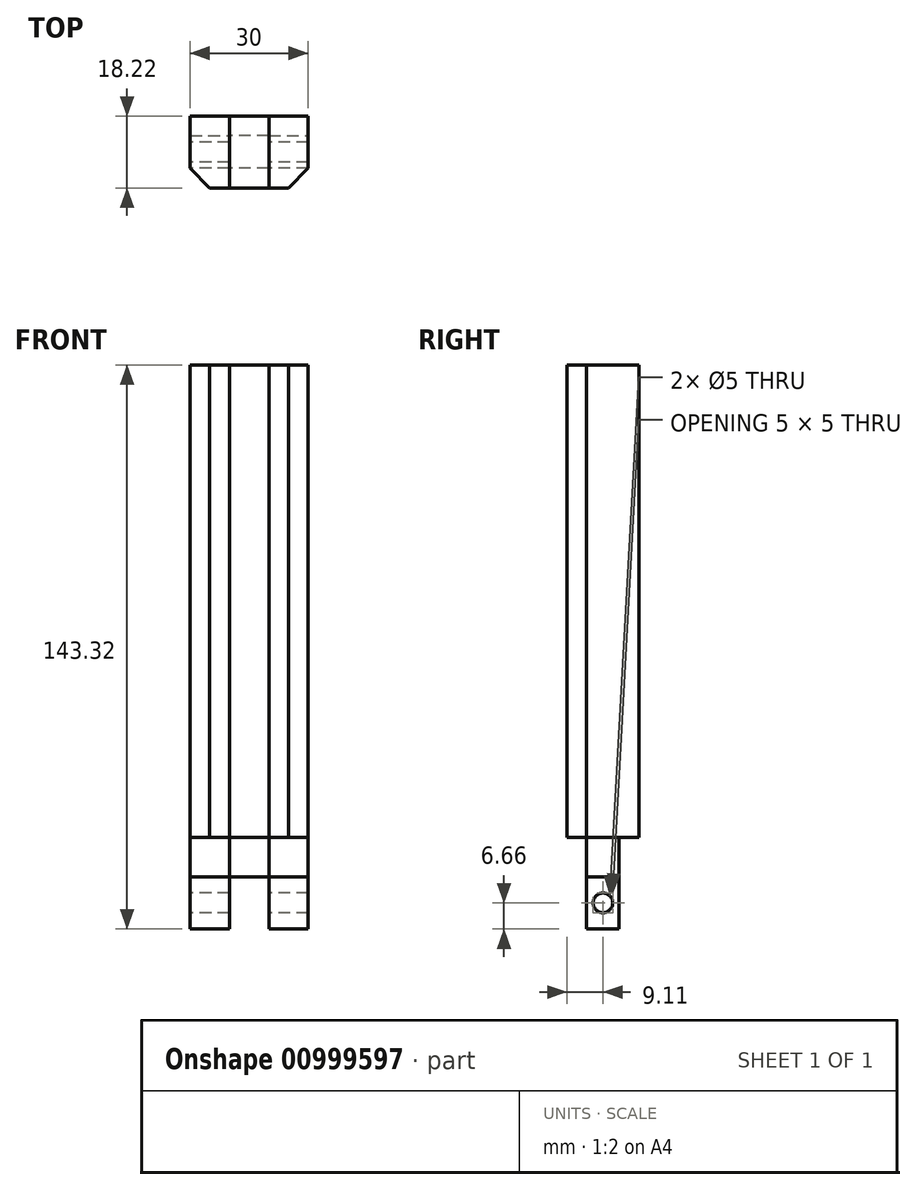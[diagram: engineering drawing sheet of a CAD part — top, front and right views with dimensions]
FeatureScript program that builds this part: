
annotation { "Feature Type Name" : "Feature", "Feature Type Description" : "" }
export const myFeature = defineFeature(function(context is Context, id is Id, definition is map)
    precondition{}
    {
        {
            var Q0;
            Q0=qCreatedBy(makeId("Right.planeOp"),FACE);
            var sketch = newSketch(context, id + "F0", { "sketchPlane" : qUnion([Q0])});
            skCircle(sketch, "E0", {"center": v(0, 0) * mm, "radius": 2.5 * mm});
            skSolve(sketch);
        }
        {
            var Q0;
            Q0=makeQuery(id+"F0.imprint","IMPRINT",FACE,{"disambiguationData":[TD([[makeQuery(id+"F0.imprint","IMPRINT",EDGE,{"derivedFrom":sQuery(id+"F0.wireOp",EDGE,"E0")}),1.0]])]});
            var sketch = newSketch(context, id + "F1", { "sketchPlane" : qUnion([Q0])});
            skLineSegment(sketch, "E1.bottom", {"start": v(9.11, 6.66) * mm, "end": v(-9.11, 6.66) * mm});
            skLineSegment(sketch, "E1.top", {"start": v(9.11, -6.66) * mm, "end": v(-9.11, -6.66) * mm});
            skLineSegment(sketch, "E1.left", {"start": v(9.11, 6.66) * mm, "end": v(9.11, -6.66) * mm});
            skLineSegment(sketch, "E1.right", {"start": v(-9.11, 6.66) * mm, "end": v(-9.11, -6.66) * mm});
            skPoint(sketch, "E1.middle", {"position": v(0, 0) * mm});
            skSolve(sketch);
        }
        {
            var Q0;
            Q0=makeQuery(id+"F1.imprint","IMPRINT",FACE,{"disambiguationData":[TD([[makeQuery(id+"F1.imprint","IMPRINT",EDGE,{"derivedFrom":sQuery(id+"F1.wireOp",EDGE,"E1.bottom")}),1.0]])]});
            extrude(context, id + "F2", {"entities" : qUnion([Q0]), "depth" : 30 * mm, "offsetDistance" : 25 * mm});
        }
        {
            var Q0;
            Q0=makeQuery(id+"F2.opExtrude","SWEPT_FACE",FACE,{"disambiguationData":[OSD([sQuery(id+"F1.wireOp",EDGE,"E1.bottom")])]});
            var sketch = newSketch(context, id + "F3", { "sketchPlane" : qUnion([Q0])});
            skLineSegment(sketch, "E2", {"start": v(10, 9.11) * mm, "end": v(10, -9.11) * mm});
            skLineSegment(sketch, "E3", {"start": v(20, 9.11) * mm, "end": v(20, -9.11) * mm});
            skSolve(sketch);
        }
        {
            var Q0;
            {var subQ0=sQuery(id+"F3.wireOp",EDGE,"E2");Q0=makeQuery(id+"F3.imprint","IMPRINT",FACE,{"disambiguationData":[TD([[makeQuery(id+"F3.imprint","IMPRINT",EDGE,{"derivedFrom":subQ0}),1.0]])]});}
            extrude(context, id + "F4", {"entities" : qUnion([Q0]), "operationType" : NewBodyOperationType.REMOVE, "oppositeDirection" : true, "depth" : 25 * mm, "offsetDistance" : 25 * mm});
        }
        {
            var Q0;
            {var subQ2=sQuery(id+"F1.wireOp",EDGE,"E1.bottom");Q0=makeQuery(id+"F4.boolean.opBoolean","SPLIT",FACE,{"disambiguationData":[TD([makeQuery(id+"F4.opExtrude","SWEPT_FACE",FACE,{"disambiguationData":[OSD([sQuery(id+"F3.wireOp",EDGE,"E2")])]})])],"derivedFrom":makeQuery(id+"F2.opExtrude","SWEPT_FACE",FACE,{"disambiguationData":[OSD([subQ2])]})});}
            var Q1;
            {var subQ2=sQuery(id+"F1.wireOp",EDGE,"E1.bottom");Q1=makeQuery(id+"F4.boolean.opBoolean","SPLIT",FACE,{"disambiguationData":[TD([makeQuery(id+"F4.opExtrude","SWEPT_FACE",FACE,{"disambiguationData":[OSD([sQuery(id+"F3.wireOp",EDGE,"E3")])]})])],"derivedFrom":makeQuery(id+"F2.opExtrude","SWEPT_FACE",FACE,{"disambiguationData":[OSD([subQ2])]})});}
            extrude(context, id + "F5", {"entities" : qUnion([Q0, Q1]), "depth" : 10 * mm, "offsetDistance" : 25 * mm});
        }
        {
            var Q0;
            Q0=makeQuery(id+"F5.opExtrude","SWEPT_FACE",FACE,{"disambiguationData":[OSD([sQuery(id+"F3.wireOp",EDGE,"E2")])]});
            extrude(context, id + "F6", {"entities" : qUnion([Q0]), "depth" : 10 * mm, "offsetDistance" : 25 * mm});
        }
        {
            var Q0;
            {var subQ2=sQuery(id+"F1.wireOp",EDGE,"E1.bottom");Q0=makeQuery(id+"F5.opExtrude","CAP_FACE",FACE,{"disambiguationData":[OSD([subQ2]),TDD([makeQuery(id+"F4.boolean.opBoolean","SPLIT",FACE,{"disambiguationData":[TD([makeQuery(id+"F4.opExtrude","SWEPT_FACE",FACE,{"disambiguationData":[OSD([sQuery(id+"F3.wireOp",EDGE,"E2")])]})])],"derivedFrom":makeQuery(id+"F2.opExtrude","SWEPT_FACE",FACE,{"disambiguationData":[OSD([subQ2])]})})])],"isStart":false});}
            var Q1;
            {var subQ0=sQuery(id+"F3.wireOp",EDGE,"E2");Q1=makeQuery(id+"F6.opExtrude","SWEPT_FACE",FACE,{"disambiguationData":[OSD([subQ0]),TDD([makeQuery(id+"F5.opExtrude","CAP_EDGE",EDGE,{"disambiguationData":[OSD([subQ0])],"isStart":false})])]});}
            var Q2;
            {var subQ2=sQuery(id+"F1.wireOp",EDGE,"E1.bottom");Q2=makeQuery(id+"F5.opExtrude","CAP_FACE",FACE,{"disambiguationData":[OSD([subQ2]),TDD([makeQuery(id+"F4.boolean.opBoolean","SPLIT",FACE,{"disambiguationData":[TD([makeQuery(id+"F4.opExtrude","SWEPT_FACE",FACE,{"disambiguationData":[OSD([sQuery(id+"F3.wireOp",EDGE,"E3")])]})])],"derivedFrom":makeQuery(id+"F2.opExtrude","SWEPT_FACE",FACE,{"disambiguationData":[OSD([subQ2])]})})])],"isStart":false});}
            extrude(context, id + "F7", {"entities" : qUnion([Q0, Q1, Q2]), "depth" : 120 * mm, "offsetDistance" : 25 * mm});
        }
        {
            var Q0;
            {var subQ0=sQuery(id+"F1.wireOp",EDGE,"E1.right");var subQ1=sQuery(id+"F1.wireOp",EDGE,"E1.bottom");Q0=makeQuery(id+"F7.opExtrude","SWEPT_EDGE",EDGE,{"disambiguationData":[OSD([subQ1,subQ0]),TDD([makeQuery(id+"F5.opExtrude","CAP_VERTEX",VERTEX,{"disambiguationData":[OSD([subQ1,subQ0]),TDD([makeQuery(id+"F2.opExtrude","CAP_VERTEX",VERTEX,{"disambiguationData":[OSD([subQ1,subQ0])],"isStart":true})])],"isStart":false})])]});}
            var Q1;
            {var subQ0=sQuery(id+"F1.wireOp",EDGE,"E1.right");var subQ1=sQuery(id+"F1.wireOp",EDGE,"E1.bottom");Q1=makeQuery(id+"F7.opExtrude","SWEPT_EDGE",EDGE,{"disambiguationData":[OSD([subQ1,subQ0]),TDD([makeQuery(id+"F5.opExtrude","CAP_VERTEX",VERTEX,{"disambiguationData":[OSD([subQ1,subQ0]),TDD([makeQuery(id+"F2.opExtrude","CAP_VERTEX",VERTEX,{"disambiguationData":[OSD([subQ1,subQ0])],"isStart":false})])],"isStart":false})])]});}
            chamfer(context, id + "F8", {"entities" : qUnion([Q0, Q1]), "width" : 5 * mm, "tangentPropagation" : true});
        }
        {
            var Q0;
            {var subQ0=sQuery(id+"F1.wireOp",EDGE,"E1.bottom");var subQ1=sQuery(id+"F1.wireOp",EDGE,"E1.right");Q0=makeQuery(id+"F5.opExtrude","SWEPT_FACE",FACE,{"disambiguationData":[OSD([subQ0,subQ1]),TDD([makeQuery(id+"F4.boolean.opBoolean","SPLIT",EDGE,{"disambiguationData":[TD([makeQuery(id+"F4.opExtrude","SWEPT_FACE",FACE,{"disambiguationData":[OSD([sQuery(id+"F3.wireOp",EDGE,"E3")])]})])],"derivedFrom":makeQuery(id+"F2.opExtrude","SWEPT_EDGE",EDGE,{"disambiguationData":[OSD([subQ0,subQ1])]})})])]});}
            var Q1;
            {var subQ1=sQuery(id+"F1.wireOp",EDGE,"E1.right");Q1=makeQuery(id+"F4.boolean.opBoolean","SPLIT",FACE,{"disambiguationData":[TD([makeQuery(id+"F4.opExtrude","SWEPT_FACE",FACE,{"disambiguationData":[OSD([sQuery(id+"F3.wireOp",EDGE,"E3")])]})])],"derivedFrom":makeQuery(id+"F2.opExtrude","SWEPT_FACE",FACE,{"disambiguationData":[OSD([subQ1])]})});}
            var Q2;
            Q2=makeQuery(id+"F6.opExtrude","SWEPT_FACE",FACE,{"disambiguationData":[OSD([sQuery(id+"F1.wireOp",EDGE,"E1.bottom"),sQuery(id+"F1.wireOp",EDGE,"E1.right"),sQuery(id+"F3.wireOp",EDGE,"E2")])]});
            var Q3;
            {var subQ1=sQuery(id+"F1.wireOp",EDGE,"E1.right");Q3=makeQuery(id+"F4.boolean.opBoolean","SPLIT",FACE,{"disambiguationData":[TD([makeQuery(id+"F4.opExtrude","SWEPT_FACE",FACE,{"disambiguationData":[OSD([sQuery(id+"F3.wireOp",EDGE,"E2")])]})])],"derivedFrom":makeQuery(id+"F2.opExtrude","SWEPT_FACE",FACE,{"disambiguationData":[OSD([subQ1])]})});}
            var Q4;
            {var subQ0=sQuery(id+"F1.wireOp",EDGE,"E1.bottom");var subQ1=sQuery(id+"F1.wireOp",EDGE,"E1.right");Q4=makeQuery(id+"F5.opExtrude","SWEPT_FACE",FACE,{"disambiguationData":[OSD([subQ0,subQ1]),TDD([makeQuery(id+"F4.boolean.opBoolean","SPLIT",EDGE,{"disambiguationData":[TD([makeQuery(id+"F4.opExtrude","SWEPT_FACE",FACE,{"disambiguationData":[OSD([sQuery(id+"F3.wireOp",EDGE,"E2")])]})])],"derivedFrom":makeQuery(id+"F2.opExtrude","SWEPT_EDGE",EDGE,{"disambiguationData":[OSD([subQ0,subQ1])]})})])]});}
            extrude(context, id + "F9", {"entities" : qUnion([Q0, Q1, Q2, Q3, Q4]), "operationType" : NewBodyOperationType.REMOVE, "oppositeDirection" : true, "depth" : 5 * mm, "offsetDistance" : 25 * mm});
        }
        {
            var Q0;
            {var subQ1=sQuery(id+"F1.wireOp",EDGE,"E1.left");Q0=makeQuery(id+"F4.boolean.opBoolean","SPLIT",FACE,{"disambiguationData":[TD([makeQuery(id+"F4.opExtrude","SWEPT_FACE",FACE,{"disambiguationData":[OSD([sQuery(id+"F3.wireOp",EDGE,"E3")])]})])],"derivedFrom":makeQuery(id+"F2.opExtrude","SWEPT_FACE",FACE,{"disambiguationData":[OSD([subQ1])]})});}
            var Q1;
            {var subQ0=sQuery(id+"F1.wireOp",EDGE,"E1.bottom");var subQ1=sQuery(id+"F1.wireOp",EDGE,"E1.left");Q1=makeQuery(id+"F5.opExtrude","SWEPT_FACE",FACE,{"disambiguationData":[OSD([subQ0,subQ1]),TDD([makeQuery(id+"F4.boolean.opBoolean","SPLIT",EDGE,{"disambiguationData":[TD([makeQuery(id+"F4.opExtrude","SWEPT_FACE",FACE,{"disambiguationData":[OSD([sQuery(id+"F3.wireOp",EDGE,"E3")])]})])],"derivedFrom":makeQuery(id+"F2.opExtrude","SWEPT_EDGE",EDGE,{"disambiguationData":[OSD([subQ0,subQ1])]})})])]});}
            var Q2;
            Q2=makeQuery(id+"F6.opExtrude","SWEPT_FACE",FACE,{"disambiguationData":[OSD([sQuery(id+"F1.wireOp",EDGE,"E1.bottom"),sQuery(id+"F1.wireOp",EDGE,"E1.left"),sQuery(id+"F3.wireOp",EDGE,"E2")])]});
            var Q3;
            {var subQ0=sQuery(id+"F1.wireOp",EDGE,"E1.bottom");var subQ1=sQuery(id+"F1.wireOp",EDGE,"E1.left");Q3=makeQuery(id+"F5.opExtrude","SWEPT_FACE",FACE,{"disambiguationData":[OSD([subQ0,subQ1]),TDD([makeQuery(id+"F4.boolean.opBoolean","SPLIT",EDGE,{"disambiguationData":[TD([makeQuery(id+"F4.opExtrude","SWEPT_FACE",FACE,{"disambiguationData":[OSD([sQuery(id+"F3.wireOp",EDGE,"E2")])]})])],"derivedFrom":makeQuery(id+"F2.opExtrude","SWEPT_EDGE",EDGE,{"disambiguationData":[OSD([subQ0,subQ1])]})})])]});}
            var Q4;
            {var subQ1=sQuery(id+"F1.wireOp",EDGE,"E1.left");Q4=makeQuery(id+"F4.boolean.opBoolean","SPLIT",FACE,{"disambiguationData":[TD([makeQuery(id+"F4.opExtrude","SWEPT_FACE",FACE,{"disambiguationData":[OSD([sQuery(id+"F3.wireOp",EDGE,"E2")])]})])],"derivedFrom":makeQuery(id+"F2.opExtrude","SWEPT_FACE",FACE,{"disambiguationData":[OSD([subQ1])]})});}
            extrude(context, id + "F10", {"entities" : qUnion([Q0, Q1, Q2, Q3, Q4]), "operationType" : NewBodyOperationType.REMOVE, "oppositeDirection" : true, "depth" : 5 * mm, "offsetDistance" : 25 * mm});
        }
    });
